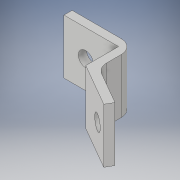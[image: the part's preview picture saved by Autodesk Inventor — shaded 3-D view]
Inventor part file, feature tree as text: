
AUTODESK INVENTOR PART (.ipt)
format: ipt  version: 2019.4 (Build 234330000, 330)  size: 131,072 bytes
history: native  units: mm
features: extrude x3, sketch x2, fillet x1
ambient origin geometry x8: Origin, YZ Plane, XZ Plane, XY Plane, X Axis, Y Axis, Z Axis, Center Point
bodies: Body1 (feature_tree)
feature tree (6):
  extrude  "Extrusion5"  Depth=20.0mm
  extrude  "Extrusion6"  Depth=18.0mm
  extrude  "Extrusion7"  TaperAngle=150.0deg  [1 undecoded]
  fillet  "Fillet1"  Radius=3.0mm
  sketch  "Sketch4"  dims[d16=12.0mm d17=20.0mm]
  sketch  "Sketch6"  dims[d18=3.0mm d19=18.0mm d20=150.0deg d21=3.0mm d24=3.0mm d25=20.0mm d26=0.0mm d27=10.0mm d28=5.5mm d29=3.0mm d30=0.0mm d31=10.0mm d32=5.5mm d33=3.0mm d34=0.0mm d35=5.0mm d36=15.0mm]
note: 1 required parameter value undecoded (feature->parameter linkage not recoverable at this tier; creation-order binding heuristic only, values carry confidence <= 0.55)
